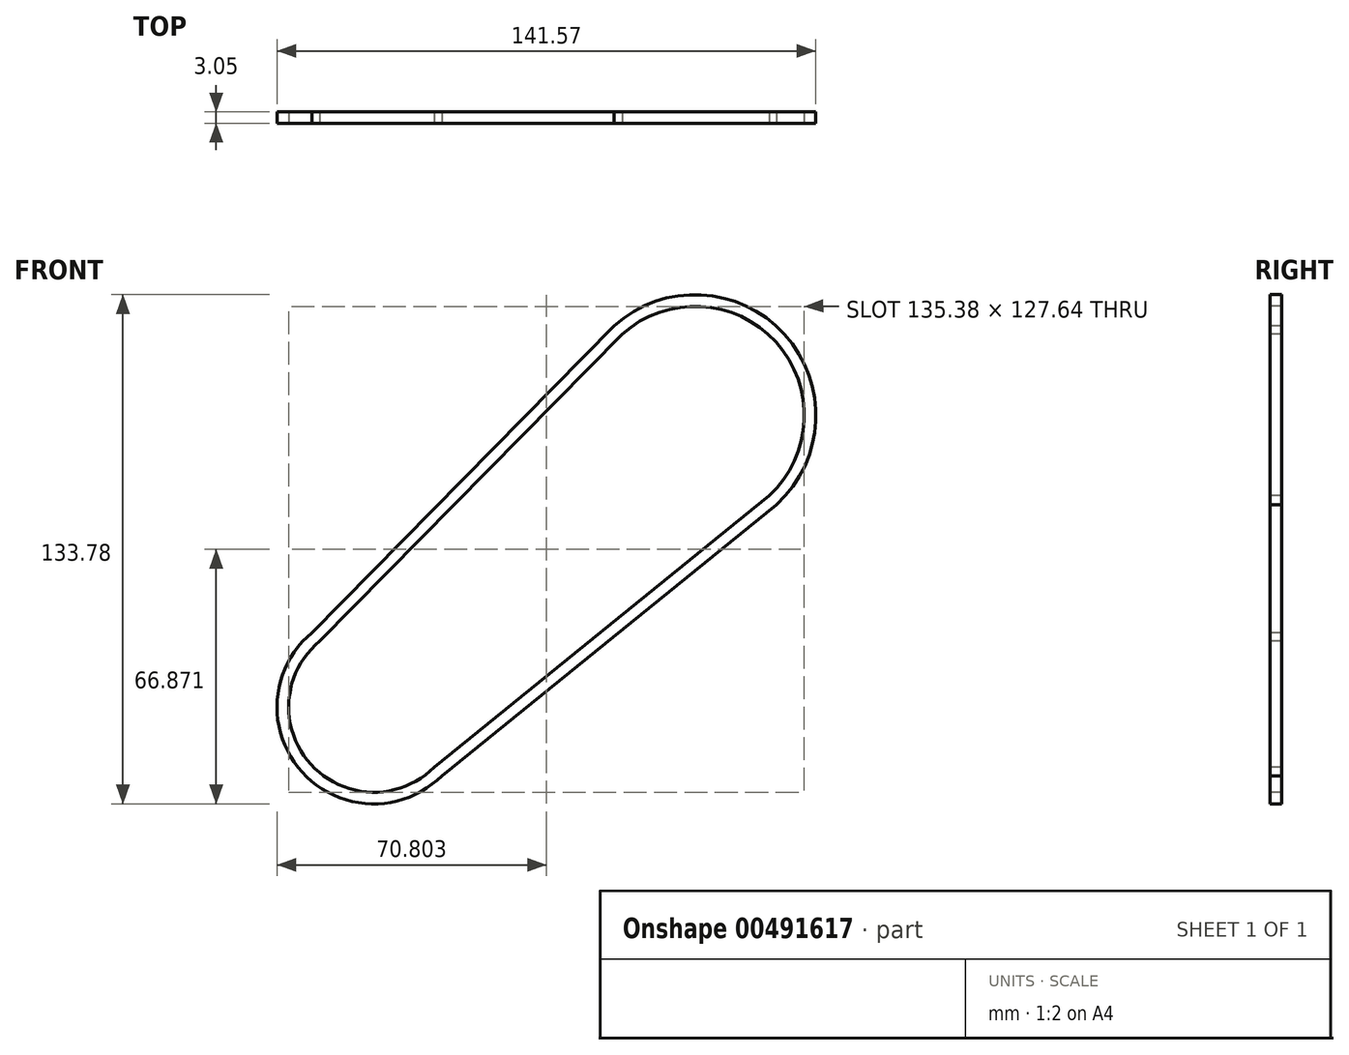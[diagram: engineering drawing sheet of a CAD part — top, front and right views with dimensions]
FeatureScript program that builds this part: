
annotation { "Feature Type Name" : "Feature", "Feature Type Description" : "" }
export const myFeature = defineFeature(function(context is Context, id is Id, definition is map)
    precondition{}
    {
        {
            var Q0;
            Q0=qCreatedBy(makeId("Front.planeOp"),FACE);
            var sketch = newSketch(context, id + "F0", { "sketchPlane" : qUnion([Q0])});
            skPoint(sketch, "E0.visualSharp", {"position": v(-60.26, -19.23) * mm});
            skPoint(sketch, "E1.visualSharp", {"position": v(-19.71, -59.18) * mm});
            skPoint(sketch, "E2.visualSharp", {"position": v(78.44, 40.46) * mm});
            skPoint(sketch, "E3.visualSharp", {"position": v(37.88, 80.4) * mm});
            skArc(sketch, "E4.1", {"start": v(-14.04, -48.97) * mm, "mid": v(-50.78, -48.04) * mm, "end": v(-48.21, -11.38) * mm});
            skArc(sketch, "E4.5", {"start": v(31.17, 69.26) * mm, "mid": v(75.91, 67.02) * mm, "end": v(73.88, 22.27) * mm});
            skLineSegment(sketch, "E5", {"start": v(-48.21, -11.38) * mm, "end": v(31.17, 69.26) * mm});
            skLineSegment(sketch, "E6", {"start": v(-14.04, -48.97) * mm, "end": v(73.88, 22.27) * mm});
            skLineSegment(sketch, "E7.0", {"start": v(-46.15, -13.63) * mm, "end": v(33.28, 67.06) * mm});
            skArc(sketch, "E7.1", {"start": v(-16.09, -46.7) * mm, "mid": v(-48.53, -46) * mm, "end": v(-46.15, -13.63) * mm});
            skLineSegment(sketch, "E7.2", {"start": v(-16.09, -46.7) * mm, "end": v(71.89, 24.58) * mm});
            skArc(sketch, "E7.3", {"start": v(33.28, 67.06) * mm, "mid": v(73.66, 64.97) * mm, "end": v(71.89, 24.58) * mm});
            skLineSegment(sketch, "E8.bottom", {"start": v(-31.97, -12.9) * mm, "end": v(-37.43, -12.9) * mm});
            skLineSegment(sketch, "E8.top", {"start": v(-31.97, -46.15) * mm, "end": v(-37.43, -46.15) * mm});
            skLineSegment(sketch, "E8.left", {"start": v(-31.97, -12.9) * mm, "end": v(-31.97, -46.15) * mm});
            skLineSegment(sketch, "E8.right", {"start": v(-37.43, -12.9) * mm, "end": v(-37.43, -46.15) * mm});
            skLineSegment(sketch, "E9", {"start": v(-8.52, 28.94) * mm, "end": v(32.4, -11.34) * mm});
            skSolve(sketch);
        }
        {
            var Q0;
            {var subQ1=sQuery(id+"F0.wireOp",EDGE,"E7.1");Q0=makeQuery(id+"F0.imprint","IMPRINT",FACE,{"disambiguationData":[TD([[makeQuery(id+"F0.imprint","IMPRINT",EDGE,{"derivedFrom":subQ1}),-1.0]])]});}
            var Q1;
            {var subQ5=sQuery(id+"F0.wireOp",EDGE,"E4.1");Q1=makeQuery(id+"F0.imprint","IMPRINT",FACE,{"disambiguationData":[TD([[makeQuery(id+"F0.imprint","IMPRINT",EDGE,{"derivedFrom":subQ5}),-1.0]])]});}
            var Q2;
            {var subQ0=sQuery(id+"F0.wireOp",EDGE,"E7.3");Q2=makeQuery(id+"F0.imprint","IMPRINT",FACE,{"disambiguationData":[TD([[makeQuery(id+"F0.imprint","IMPRINT",EDGE,{"derivedFrom":subQ0}),-1.0]])]});}
            var Q3;
            {var subQ8=sQuery(id+"F0.wireOp",EDGE,"E4.5");Q3=makeQuery(id+"F0.imprint","IMPRINT",FACE,{"disambiguationData":[TD([[makeQuery(id+"F0.imprint","IMPRINT",EDGE,{"derivedFrom":subQ8}),-1.0]])]});}
            extrude(context, id + "F1", {"entities" : qUnion([Q0, Q1, Q2, Q3]), "oppositeDirection" : true, "depth" : 3.05 * mm});
        }
    });
